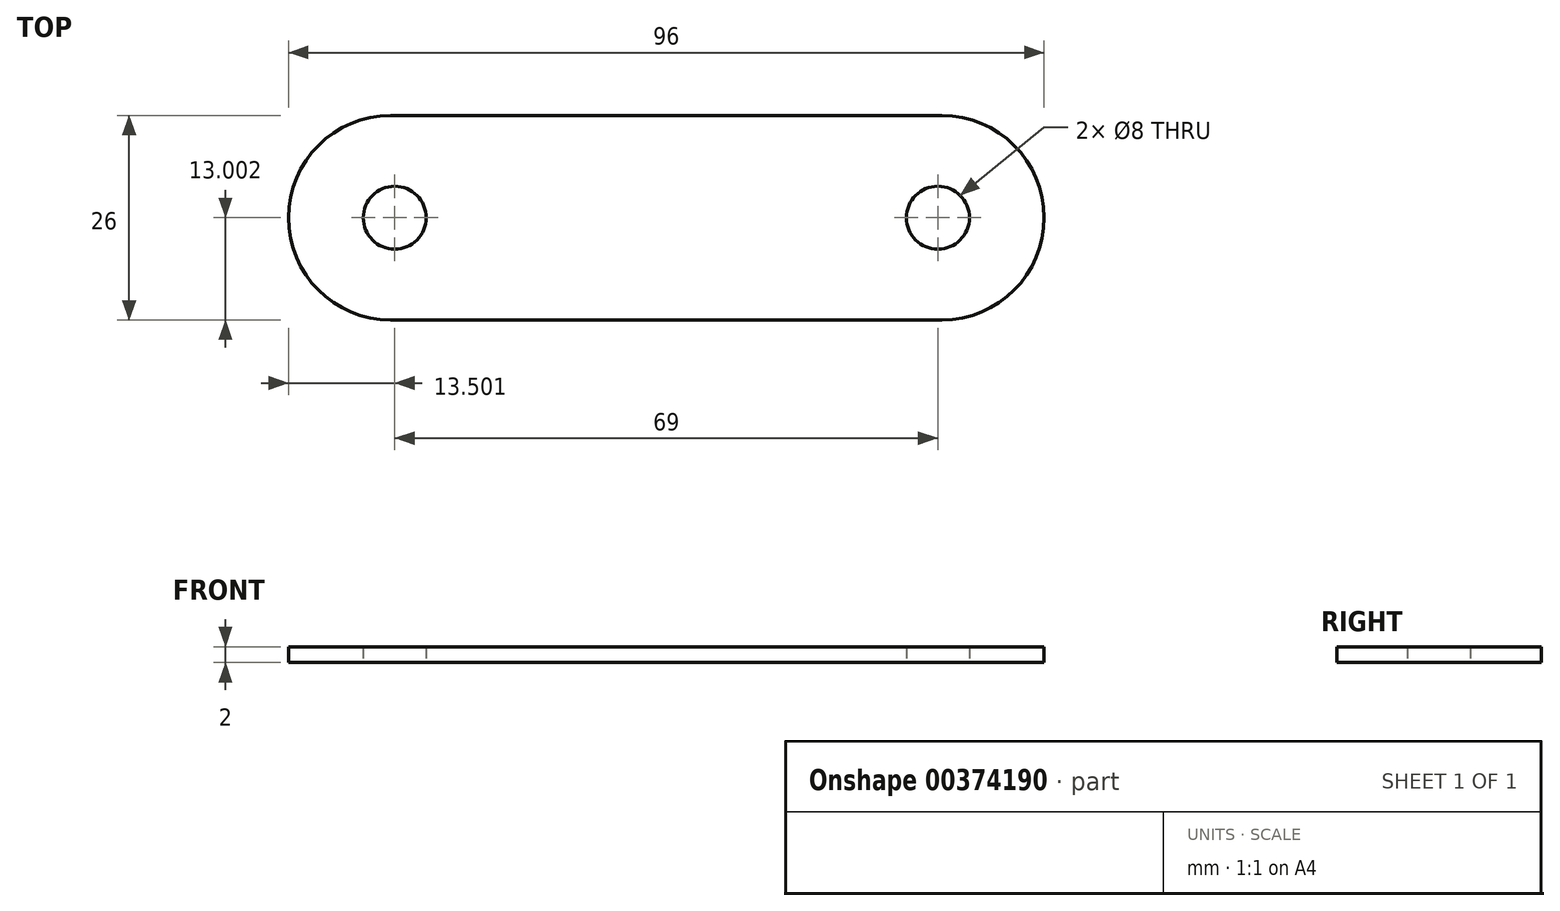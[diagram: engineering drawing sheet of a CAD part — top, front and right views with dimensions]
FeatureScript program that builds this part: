
annotation { "Feature Type Name" : "Feature", "Feature Type Description" : "" }
export const myFeature = defineFeature(function(context is Context, id is Id, definition is map)
    precondition{}
    {
        {
            var Q0;
            Q0=qCreatedBy(makeId("Top.planeOp"),FACE);
            var sketch = newSketch(context, id + "F0", { "sketchPlane" : qUnion([Q0])});
            skLineSegment(sketch, "E0.bottom", {"start": v(-32.82, 7.62) * mm, "end": v(37.18, 7.62) * mm});
            skLineSegment(sketch, "E0.top", {"start": v(-32.82, -18.38) * mm, "end": v(37.18, -18.38) * mm});
            skLineSegment(sketch, "E0.left", {"start": v(-45.82, -5.38) * mm, "end": v(-45.82, -5.38) * mm});
            skLineSegment(sketch, "E0.right", {"start": v(50.18, -5.38) * mm, "end": v(50.18, -5.38) * mm});
            skLineSegment(sketch, "E1", {"start": v(2.18, 7.62) * mm, "end": v(2.18, -18.38) * mm, "construction": true});
            skLineSegment(sketch, "E2", {"start": v(-45.82, -5.38) * mm, "end": v(-36.32, -5.38) * mm, "construction": true});
            skLineSegment(sketch, "E3", {"start": v(-45.82, -5.38) * mm, "end": v(50.18, -5.38) * mm, "construction": true});
            skCircle(sketch, "E4", {"center": v(-32.32, -5.38) * mm, "radius": 4 * mm});
            skCircle(sketch, "E5.MirrorC", {"center": v(36.68, -5.38) * mm, "radius": 4 * mm});
            skPoint(sketch, "E6.visualSharp", {"position": v(-45.82, 7.62) * mm});
            skArc(sketch, "E6.filletArc", {"start": v(-32.82, 7.62) * mm, "mid": v(-42.01, 3.81) * mm, "end": v(-45.82, -5.38) * mm});
            skPoint(sketch, "E7.visualSharp", {"position": v(-45.82, -18.38) * mm});
            skArc(sketch, "E7.filletArc", {"start": v(-45.82, -5.38) * mm, "mid": v(-42.01, -14.57) * mm, "end": v(-32.82, -18.38) * mm});
            skPoint(sketch, "E8.visualSharp", {"position": v(50.18, -18.38) * mm});
            skArc(sketch, "E8.filletArc", {"start": v(37.18, -18.38) * mm, "mid": v(46.37, -14.57) * mm, "end": v(50.18, -5.38) * mm});
            skPoint(sketch, "E9.visualSharp", {"position": v(50.18, 7.62) * mm});
            skArc(sketch, "E9.filletArc", {"start": v(50.18, -5.38) * mm, "mid": v(46.37, 3.81) * mm, "end": v(37.18, 7.62) * mm});
            skSolve(sketch);
        }
        {
            var Q0;
            Q0=makeQuery(id+"F0.imprint","IMPRINT",FACE,{"disambiguationData":[TD([[makeQuery(id+"F0.imprint","IMPRINT",EDGE,{"derivedFrom":sQuery(id+"F0.wireOp",EDGE,"E0.bottom")}),-1.0]])]});
            extrude(context, id + "F1", {"entities" : qUnion([Q0]), "depth" : 2 * mm});
        }
    });
